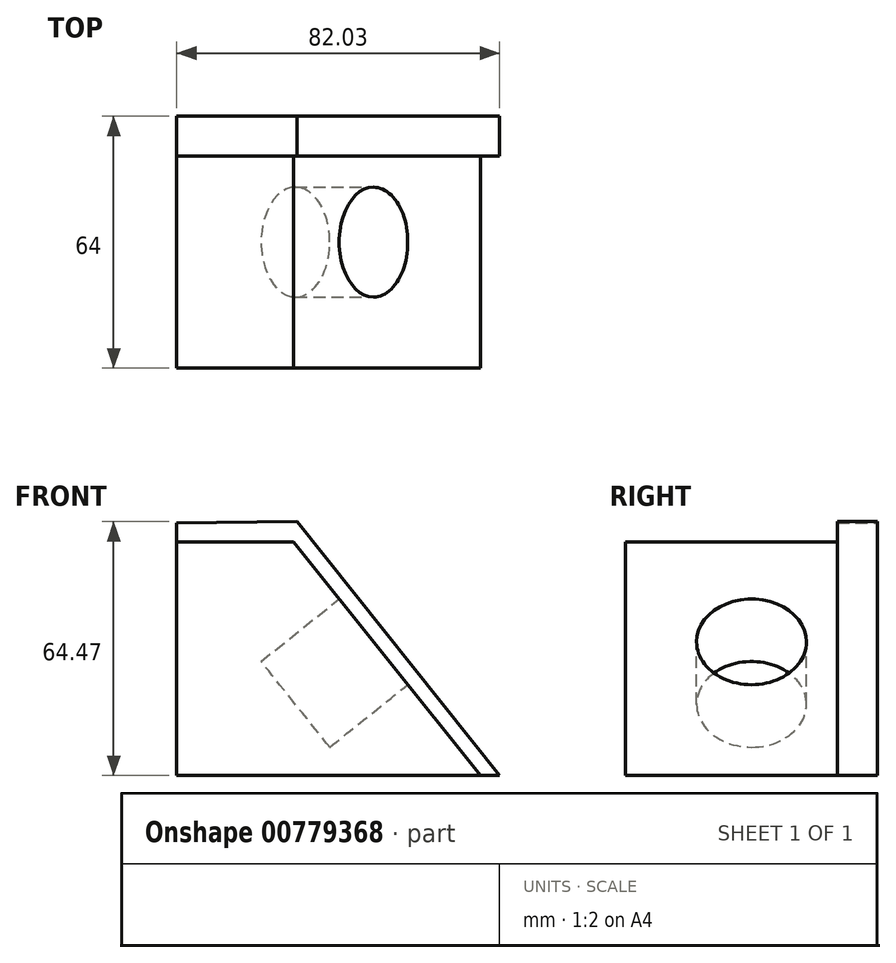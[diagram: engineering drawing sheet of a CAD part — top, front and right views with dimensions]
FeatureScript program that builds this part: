
annotation { "Feature Type Name" : "Feature", "Feature Type Description" : "" }
export const myFeature = defineFeature(function(context is Context, id is Id, definition is map)
    precondition{}
    {
        {
            var Q0;
            Q0=qCreatedBy(makeId("Front.planeOp"),FACE);
            var sketch = newSketch(context, id + "F0", { "sketchPlane" : qUnion([Q0])});
            skLineSegment(sketch, "E0", {"start": v(-44.47, 34.68) * mm, "end": v(-44.47, -29.5) * mm});
            skLineSegment(sketch, "E1", {"start": v(-44.47, -29.5) * mm, "end": v(37.56, -29.5) * mm});
            skLineSegment(sketch, "E2", {"start": v(37.56, -29.5) * mm, "end": v(-13.96, 34.97) * mm});
            skLineSegment(sketch, "E3", {"start": v(-13.96, 34.97) * mm, "end": v(-44.47, 34.68) * mm});
            skSolve(sketch);
        }
        {
            var Q0;
            Q0=makeQuery(id+"F0.imprint","IMPRINT",FACE,{"disambiguationData":[TD([[makeQuery(id+"F0.imprint","IMPRINT",EDGE,{"derivedFrom":sQuery(id+"F0.wireOp",EDGE,"E0")}),1.0]])]});
            extrude(context, id + "F1", {"entities" : qUnion([Q0]), "depth" : 32 * mm, "offsetDistance" : 25.4 * mm});
        }
        {
            var Q0;
            Q0=makeQuery(id+"F1.opExtrude","CAP_FACE",FACE,{"disambiguationData":[OSD([sQuery(id+"F0.wireOp",EDGE,"E0"),sQuery(id+"F0.wireOp",EDGE,"E1"),sQuery(id+"F0.wireOp",EDGE,"E2"),sQuery(id+"F0.wireOp",EDGE,"E3")])],"isStart":true});
            extrude(context, id + "F2", {"entities" : qUnion([Q0]), "operationType" : NewBodyOperationType.ADD, "depth" : 32 * mm, "offsetDistance" : 25.4 * mm});
        }
        {
            var Q0;
            Q0=makeQuery(id+"F1.opExtrude","CAP_FACE",FACE,{"disambiguationData":[OSD([sQuery(id+"F0.wireOp",EDGE,"E0"),sQuery(id+"F0.wireOp",EDGE,"E1"),sQuery(id+"F0.wireOp",EDGE,"E2"),sQuery(id+"F0.wireOp",EDGE,"E3")])],"isStart":false});
            var sketch = newSketch(context, id + "F3", { "sketchPlane" : qUnion([Q0])});
            skLineSegment(sketch, "E4", {"start": v(-44.47, 29.79) * mm, "end": v(-14.82, 29.79) * mm});
            skLineSegment(sketch, "E5", {"start": v(-14.82, 29.79) * mm, "end": v(32.67, -29.5) * mm});
            skLineSegment(sketch, "E6", {"start": v(32.67, -29.5) * mm, "end": v(37.56, -29.5) * mm});
            skLineSegment(sketch, "E7", {"start": v(37.56, -29.5) * mm, "end": v(-13.96, 34.97) * mm});
            skLineSegment(sketch, "E8", {"start": v(-13.96, 34.97) * mm, "end": v(-44.47, 34.68) * mm});
            skLineSegment(sketch, "E9", {"start": v(-44.47, 34.68) * mm, "end": v(-44.47, 29.79) * mm});
            skSolve(sketch);
        }
        {
            var Q0;
            Q0=makeQuery(id+"F3.imprint","IMPRINT",FACE,{"disambiguationData":[TD([[makeQuery(id+"F3.imprint","IMPRINT",EDGE,{"derivedFrom":sQuery(id+"F3.wireOp",EDGE,"E4")}),1.0]])]});
            extrude(context, id + "F4", {"entities" : qUnion([Q0]), "operationType" : NewBodyOperationType.REMOVE, "oppositeDirection" : true, "depth" : 53.85 * mm, "offsetDistance" : 25.4 * mm});
        }
        {
            var Q0;
            Q0=makeQuery(id+"F4.boolean.opBoolean","COPY",FACE,{"derivedFrom":makeQuery(id+"F4.opExtrude","SWEPT_FACE",FACE,{"disambiguationData":[OSD([sQuery(id+"F3.wireOp",EDGE,"E5")])]})});
            var sketch = newSketch(context, id + "F5", { "sketchPlane" : qUnion([Q0])});
            skCircle(sketch, "E10", {"center": v(0, 0) * mm, "radius": 13.95 * mm});
            skSolve(sketch);
        }
        {
            var Q0;
            Q0=makeQuery(id+"F5.imprint","IMPRINT",FACE,{"disambiguationData":[TD([[makeQuery(id+"F5.imprint","IMPRINT",EDGE,{"derivedFrom":sQuery(id+"F5.wireOp",EDGE,"E10")}),1.0]])]});
            extrude(context, id + "F6", {"entities" : qUnion([Q0]), "operationType" : NewBodyOperationType.REMOVE, "oppositeDirection" : true, "depth" : 25.4 * mm, "offsetDistance" : 25.4 * mm});
        }
    });
